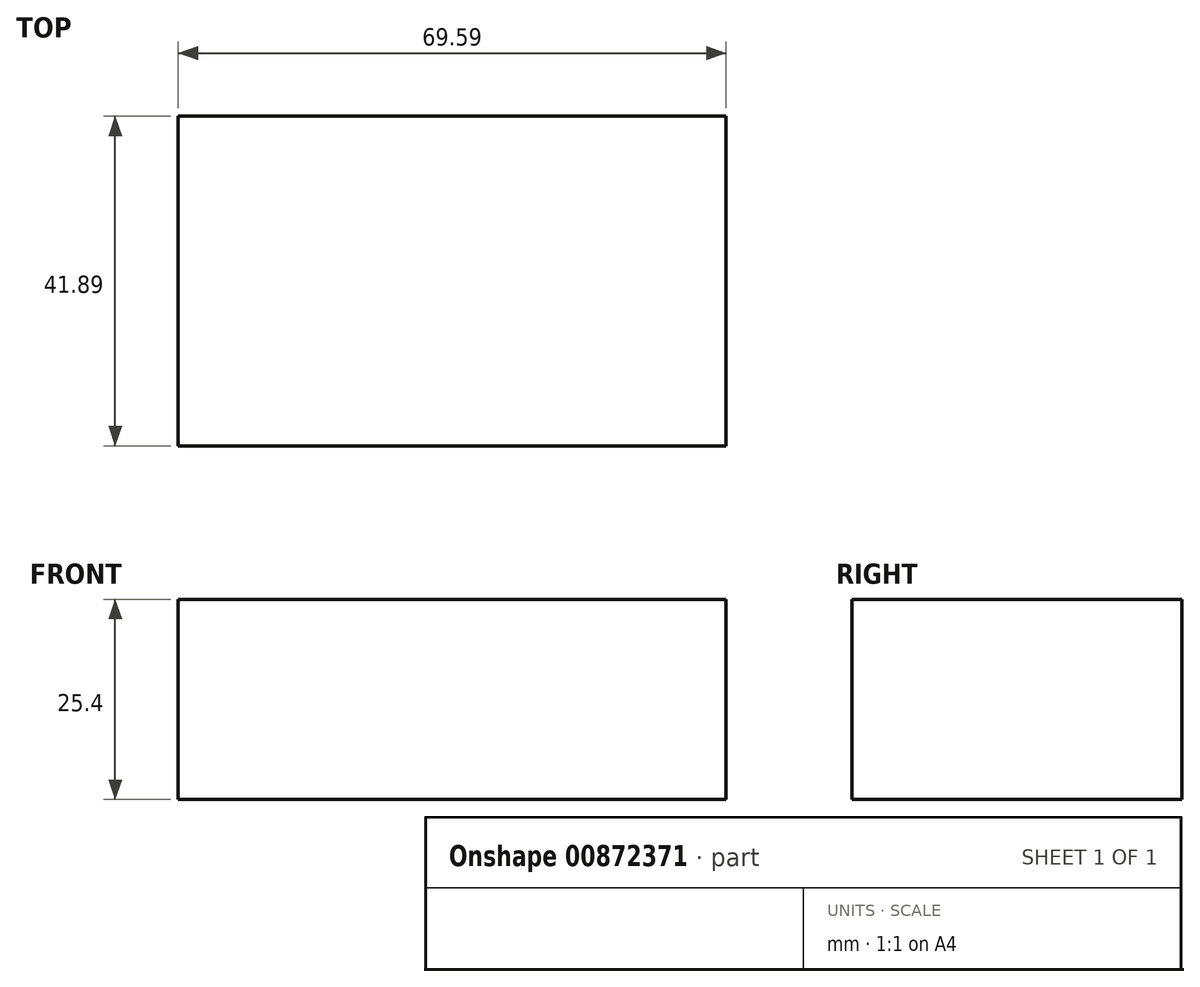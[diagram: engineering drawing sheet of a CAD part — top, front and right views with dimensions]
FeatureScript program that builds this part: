
annotation { "Feature Type Name" : "Feature", "Feature Type Description" : "" }
export const myFeature = defineFeature(function(context is Context, id is Id, definition is map)
    precondition{}
    {
        {
            var Q0;
            Q0=qCreatedBy(makeId("Top.planeOp"),FACE);
            var sketch = newSketch(context, id + "F0", { "sketchPlane" : qUnion([Q0])});
            skLineSegment(sketch, "E0.bottom", {"start": v(-69.6, 14.4) * mm, "end": v(0, 14.4) * mm});
            skLineSegment(sketch, "E0.top", {"start": v(-69.6, -27.49) * mm, "end": v(0, -27.49) * mm});
            skLineSegment(sketch, "E0.left", {"start": v(-69.6, 14.4) * mm, "end": v(-69.6, -27.49) * mm});
            skLineSegment(sketch, "E0.right", {"start": v(0, 14.4) * mm, "end": v(0, -27.49) * mm});
            skSolve(sketch);
        }
        {
            var Q0;
            Q0=makeQuery(id+"F0.imprint","IMPRINT",FACE,{"disambiguationData":[TD([[makeQuery(id+"F0.imprint","IMPRINT",EDGE,{"derivedFrom":sQuery(id+"F0.wireOp",EDGE,"E0.bottom")}),-1.0]])]});
            extrude(context, id + "F1", {"entities" : qUnion([Q0]), "depth" : 25.4 * mm, "offsetDistance" : 25.4 * mm});
        }
        {
            var Q0;
            Q0=makeQuery(id+"F1.opExtrude","SWEPT_FACE",FACE,{"disambiguationData":[OSD([sQuery(id+"F0.wireOp",EDGE,"E0.right")])]});
            extrude(context, id + "F2", {"entities" : qUnion([Q0]), "operationType" : NewBodyOperationType.ADD, "oppositeDirection" : true, "depth" : 69.6 * mm, "offsetDistance" : 25.4 * mm});
        }
        {
            var Q0;
            Q0=sQuery(id+"F0.wireOp",EDGE,"E0.top");
            extrude(context, id + "F3", {"bodyType" : ToolBodyType.SURFACE, "surfaceEntities" : qUnion([Q0]), "depth" : 25 * mm, "offsetDistance" : 25 * mm});
        }
    });
